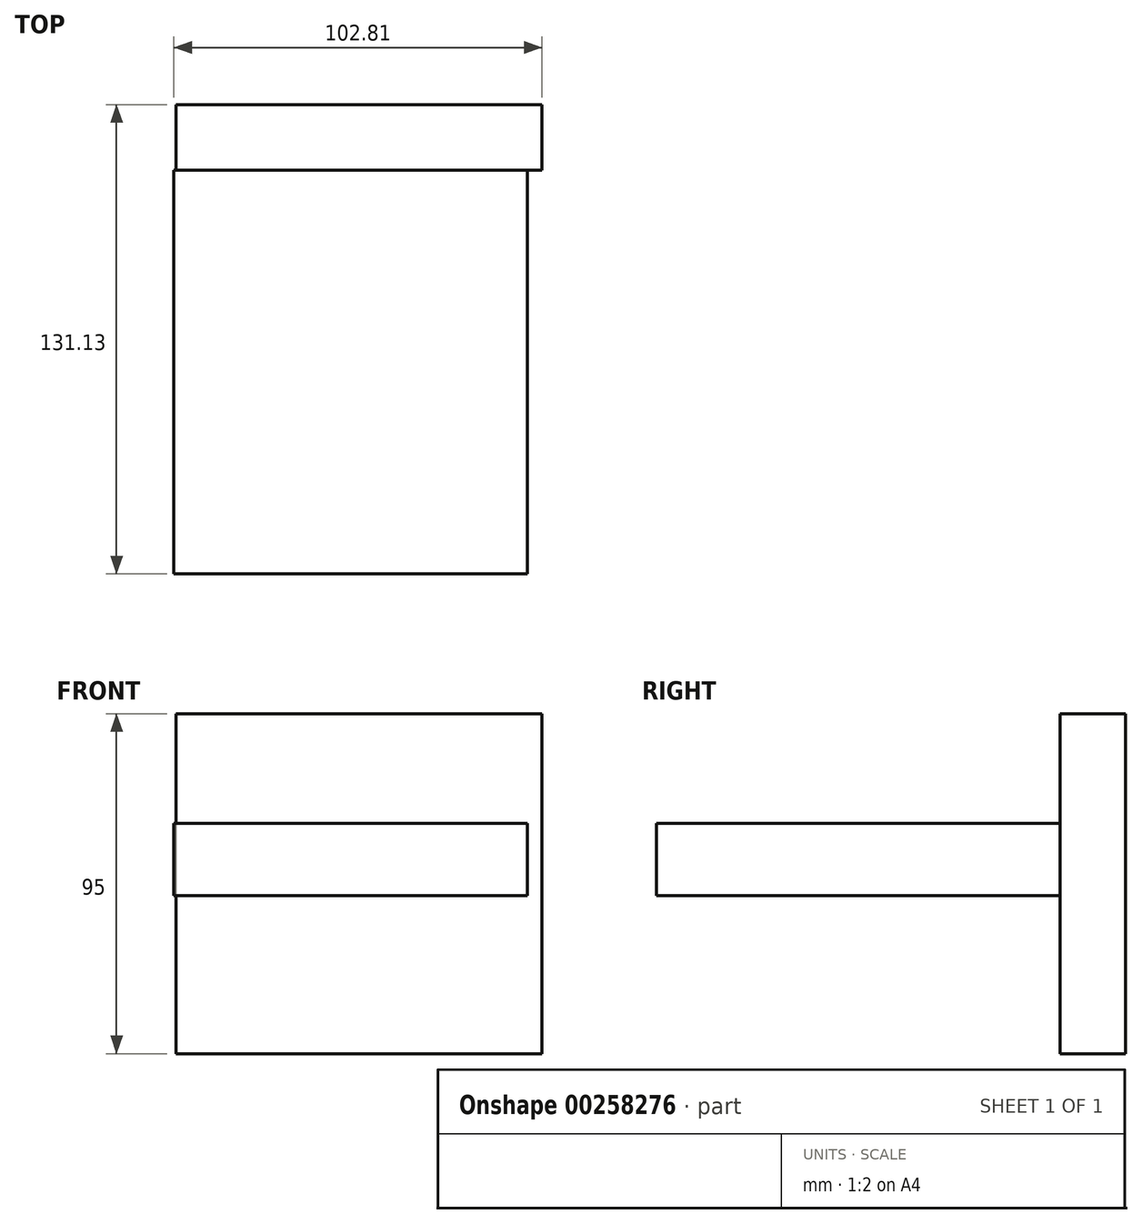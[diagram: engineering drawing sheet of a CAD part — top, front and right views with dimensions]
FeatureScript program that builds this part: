
annotation { "Feature Type Name" : "Feature", "Feature Type Description" : "" }
export const myFeature = defineFeature(function(context is Context, id is Id, definition is map)
    precondition{}
    {
        {
            var Q0;
            Q0=qCreatedBy(makeId("Top.planeOp"),FACE);
            var sketch = newSketch(context, id + "F0", { "sketchPlane" : qUnion([Q0])});
            skLineSegment(sketch, "E0.bottom", {"start": v(-65.98, 0) * mm, "end": v(36.2, 0) * mm});
            skLineSegment(sketch, "E0.top", {"start": v(-65.98, 18.35) * mm, "end": v(36.2, 18.35) * mm});
            skLineSegment(sketch, "E0.left", {"start": v(-65.98, 0) * mm, "end": v(-65.98, 18.35) * mm});
            skLineSegment(sketch, "E0.right", {"start": v(36.2, 0) * mm, "end": v(36.2, 18.35) * mm});
            skSolve(sketch);
        }
        {
            var Q0;
            Q0 = qSketchRegion(id + "F0", true);
            extrude(context, id + "F1", {"entities" : qUnion([Q0]), "oppositeDirection" : true, "depth" : 95 * mm});
        }
        {
            var Q0;
            Q0=qCreatedBy(makeId("Front.planeOp"),FACE);
            var sketch = newSketch(context, id + "F2", { "sketchPlane" : qUnion([Q0])});
            skLineSegment(sketch, "E1.bottom", {"start": v(-66.6, -50.85) * mm, "end": v(32.1, -50.85) * mm});
            skLineSegment(sketch, "E1.top", {"start": v(-66.6, -30.66) * mm, "end": v(32.1, -30.66) * mm});
            skLineSegment(sketch, "E1.left", {"start": v(-66.6, -50.85) * mm, "end": v(-66.6, -30.66) * mm});
            skLineSegment(sketch, "E1.right", {"start": v(32.1, -50.85) * mm, "end": v(32.1, -30.66) * mm});
            skSolve(sketch);
        }
        {
            var Q0;
            Q0=makeQuery(id+"F2.imprint","IMPRINT",FACE,{"disambiguationData":[TD([[makeQuery(id+"F2.imprint","IMPRINT",EDGE,{"derivedFrom":sQuery(id+"F2.wireOp",EDGE,"E1.bottom")}),1.0]])]});
            extrude(context, id + "F3", {"entities" : qUnion([Q0]), "operationType" : NewBodyOperationType.ADD, "depth" : 112.78 * mm});
        }
    });
